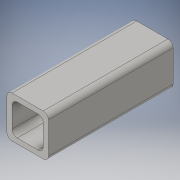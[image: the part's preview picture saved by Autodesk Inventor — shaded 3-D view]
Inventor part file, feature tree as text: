
AUTODESK INVENTOR PART (.ipt)
format: ipt  version: 2016 (Build 200138000, 138)  size: 112,640 bytes
history: native  units: in
note: dims shown in document units (in); Inventor stores cm internally (conversion verified against a paired STEP export)
features: extrude x1, sketch x1
ambient origin geometry x8: Origin, YZ Plane, XZ Plane, XY Plane, X Axis, Y Axis, Z Axis, Center Point
bodies: Solid1 (feature_tree)
feature tree (2):
  extrude  "Extrusion1"  Depth=1.0in
  sketch  "Sketch1"  dims[d0=1.0in d1=1.0in d2=0.125in d3=0.125in d4=3.0in d5=0.0in]
